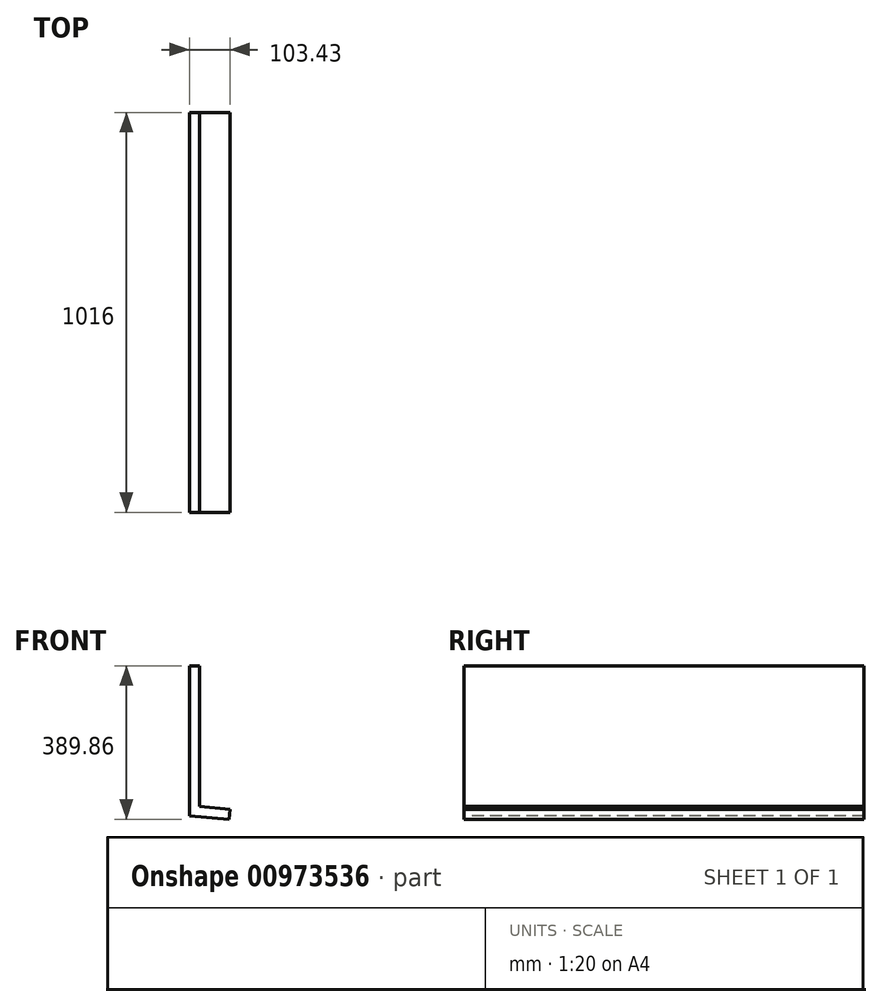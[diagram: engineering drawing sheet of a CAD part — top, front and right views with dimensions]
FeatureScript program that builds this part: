
annotation { "Feature Type Name" : "Feature", "Feature Type Description" : "" }
export const myFeature = defineFeature(function(context is Context, id is Id, definition is map)
    precondition{}
    {
        {
            var Q0;
            Q0=qCreatedBy(makeId("Right.planeOp"),FACE);
            var sketch = newSketch(context, id + "F0", { "sketchPlane" : qUnion([Q0])});
            skLineSegment(sketch, "E0.bottom", {"start": v(508, -190.5) * mm, "end": v(-508, -190.5) * mm});
            skLineSegment(sketch, "E0.top", {"start": v(508, 190.5) * mm, "end": v(-508, 190.5) * mm});
            skLineSegment(sketch, "E0.left", {"start": v(508, -190.5) * mm, "end": v(508, 190.5) * mm});
            skLineSegment(sketch, "E0.right", {"start": v(-508, -190.5) * mm, "end": v(-508, 190.5) * mm});
            skPoint(sketch, "E0.middle", {"position": v(0, 0) * mm});
            skSolve(sketch);
        }
        {
            var Q0;
            Q0 = qSketchRegion(id + "F0", true);
            extrude(context, id + "F1", {"entities" : qUnion([Q0]), "depth" : 25.4 * mm, "offsetDistance" : 25.4 * mm});
        }
        {
            var Q0;
            Q0=makeQuery(id+"F1.opExtrude","SWEPT_FACE",FACE,{"disambiguationData":[OSD([sQuery(id+"F0.wireOp",EDGE,"E0.right")])]});
            var sketch = newSketch(context, id + "F2", { "sketchPlane" : qUnion([Q0])});
            skLineSegment(sketch, "E1", {"start": v(0, -190.5) * mm, "end": v(101.21, -199.36) * mm});
            skLineSegment(sketch, "E2", {"start": v(101.21, -199.36) * mm, "end": v(103.43, -174.05) * mm});
            skLineSegment(sketch, "E3", {"start": v(103.43, -174.05) * mm, "end": v(0, -165) * mm});
            skLineSegment(sketch, "E4", {"start": v(0, -165) * mm, "end": v(0, -190.5) * mm});
            skSolve(sketch);
        }
        {
            var Q0;
            Q0 = qSketchRegion(id + "F2", true);
            var Q1;
            Q1=makeQuery(id+"F1.opExtrude","SWEPT_FACE",FACE,{"disambiguationData":[OSD([sQuery(id+"F0.wireOp",EDGE,"E0.left")])]});
            extrude(context, id + "F3", {"entities" : qUnion([Q0]), "operationType" : NewBodyOperationType.ADD, "endBound" : BoundingType.UP_TO_SURFACE, "oppositeDirection" : true, "depth" : 25.4 * mm, "endBoundEntityFace" : qUnion([Q1]), "offsetDistance" : 25.4 * mm});
        }
    });
